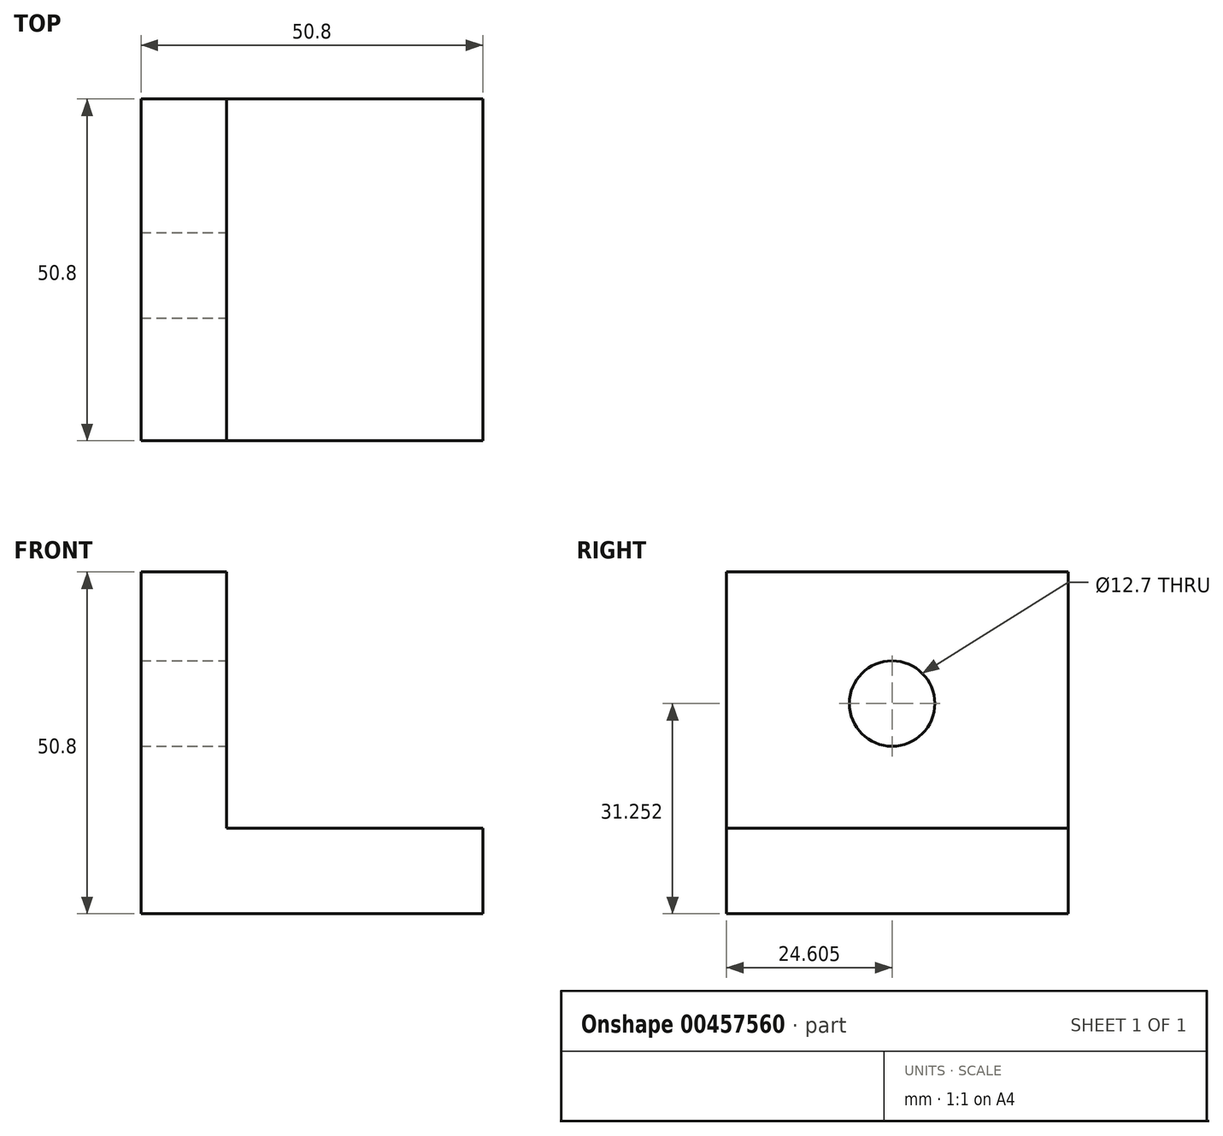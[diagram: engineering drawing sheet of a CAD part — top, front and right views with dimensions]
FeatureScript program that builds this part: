
annotation { "Feature Type Name" : "Feature", "Feature Type Description" : "" }
export const myFeature = defineFeature(function(context is Context, id is Id, definition is map)
    precondition{}
    {
        {
            var Q0;
            Q0=qCreatedBy(makeId("Top.planeOp"),FACE);
            var sketch = newSketch(context, id + "F0", { "sketchPlane" : qUnion([Q0])});
            skLineSegment(sketch, "E0.bottom", {"start": v(0, 0) * mm, "end": v(12.7, 0) * mm});
            skLineSegment(sketch, "E0.top", {"start": v(0, -50.8) * mm, "end": v(12.7, -50.8) * mm});
            skLineSegment(sketch, "E0.left", {"start": v(0, 0) * mm, "end": v(0, -50.8) * mm});
            skLineSegment(sketch, "E0.right", {"start": v(12.7, 0) * mm, "end": v(12.7, -50.8) * mm});
            skSolve(sketch);
        }
        {
            var Q0;
            Q0 = qSketchRegion(id + "F0", true);
            extrude(context, id + "F1", {"entities" : qUnion([Q0]), "depth" : 50.8 * mm});
        }
        {
            var Q0;
            Q0=qCreatedBy(makeId("Right.planeOp"),FACE);
            var sketch = newSketch(context, id + "F2", { "sketchPlane" : qUnion([Q0])});
            skLineSegment(sketch, "E1.bottom", {"start": v(0, 0) * mm, "end": v(-50.8, 0) * mm});
            skLineSegment(sketch, "E1.top", {"start": v(0, 12.7) * mm, "end": v(-50.8, 12.7) * mm});
            skLineSegment(sketch, "E1.left", {"start": v(0, 0) * mm, "end": v(0, 12.7) * mm});
            skLineSegment(sketch, "E1.right", {"start": v(-50.8, 0) * mm, "end": v(-50.8, 12.7) * mm});
            skSolve(sketch);
        }
        {
            var Q0;
            Q0 = qSketchRegion(id + "F2", true);
            extrude(context, id + "F3", {"entities" : qUnion([Q0]), "operationType" : NewBodyOperationType.ADD, "depth" : 50.8 * mm});
        }
        {
            var Q0;
            Q0=makeQuery(id+"F1.opExtrude","SWEPT_FACE",FACE,{"disambiguationData":[OSD([sQuery(id+"F0.wireOp",EDGE,"E0.right")])]});
            var sketch = newSketch(context, id + "F4", { "sketchPlane" : qUnion([Q0])});
            skCircle(sketch, "E2", {"center": v(-26.2, 31.25) * mm, "radius": 6.35 * mm});
            skSolve(sketch);
        }
        {
            var Q0;
            Q0=makeQuery(id+"F4.imprint","IMPRINT",FACE,{"disambiguationData":[TD([[makeQuery(id+"F4.imprint","IMPRINT",EDGE,{"derivedFrom":sQuery(id+"F4.wireOp",EDGE,"E2")}),1.0]])]});
            extrude(context, id + "F5", {"entities" : qUnion([Q0]), "operationType" : NewBodyOperationType.REMOVE, "endBound" : BoundingType.THROUGH_ALL, "oppositeDirection" : true, "depth" : 25.4 * mm});
        }
    });
